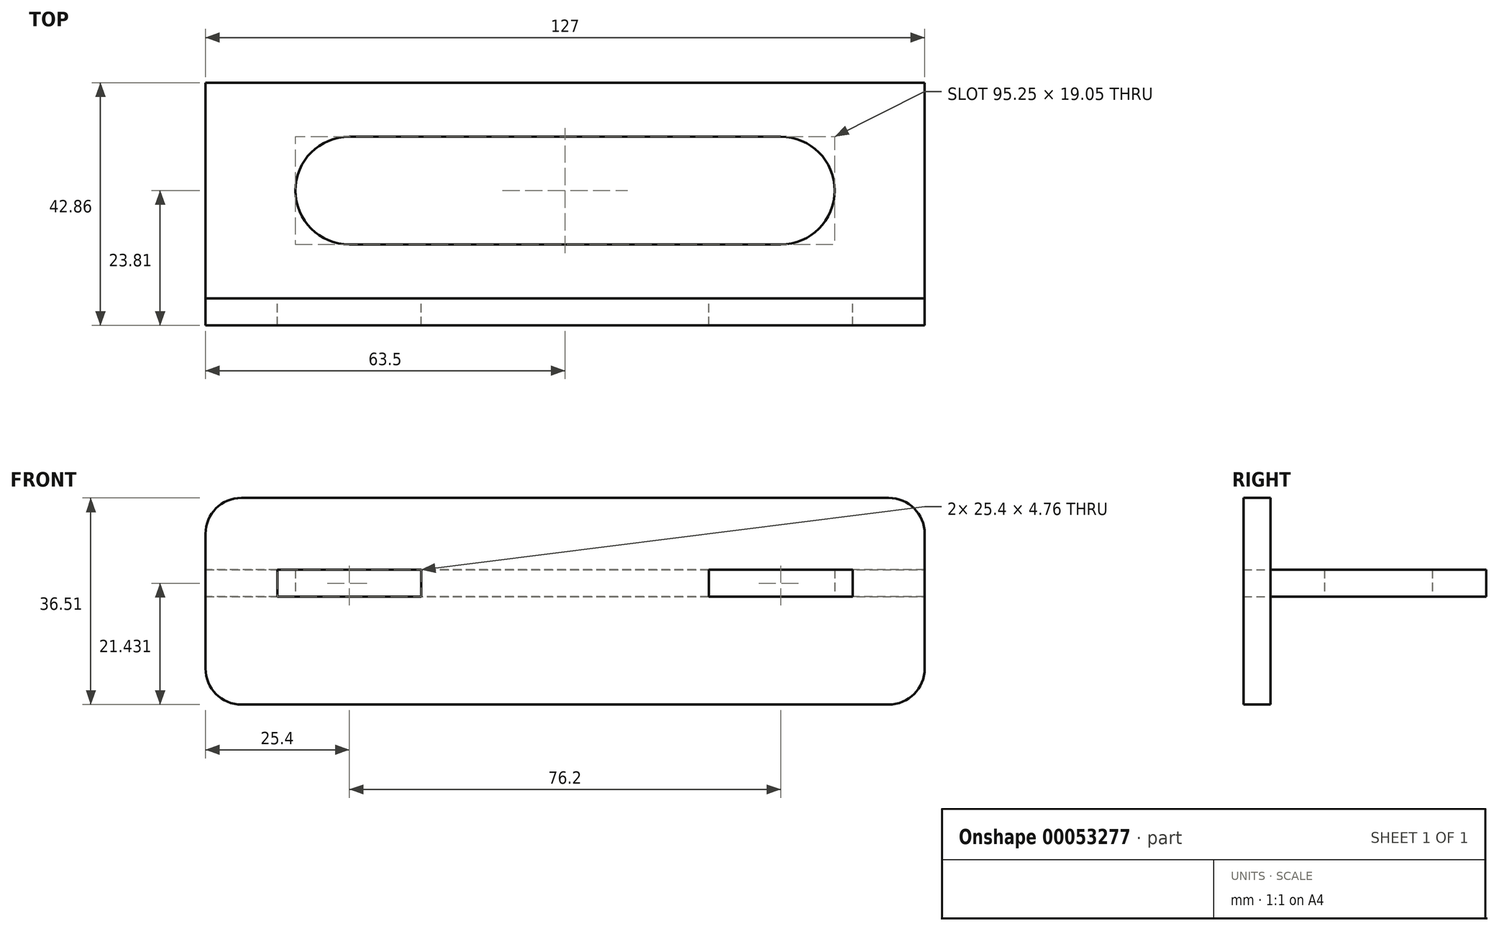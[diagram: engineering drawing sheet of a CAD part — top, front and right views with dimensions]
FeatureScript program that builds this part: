
annotation { "Feature Type Name" : "Feature", "Feature Type Description" : "" }
export const myFeature = defineFeature(function(context is Context, id is Id, definition is map)
    precondition{}
    {
        {
            var Q0;
            Q0=qCreatedBy(makeId("Top.planeOp"),FACE);
            var sketch = newSketch(context, id + "F0", { "sketchPlane" : qUnion([Q0])});
            skLineSegment(sketch, "E0", {"start": v(-101.6, 19.05) * mm, "end": v(25.4, 19.05) * mm});
            skLineSegment(sketch, "E1", {"start": v(25.4, 19.05) * mm, "end": v(25.4, -19.05) * mm});
            skLineSegment(sketch, "E2", {"start": v(25.4, -19.05) * mm, "end": v(12.7, -19.05) * mm});
            skLineSegment(sketch, "E3", {"start": v(12.7, -19.05) * mm, "end": v(12.7, -23.81) * mm});
            skLineSegment(sketch, "E4", {"start": v(12.7, -23.81) * mm, "end": v(-12.7, -23.81) * mm});
            skLineSegment(sketch, "E5", {"start": v(-12.7, -23.81) * mm, "end": v(-12.7, -19.05) * mm});
            skLineSegment(sketch, "E6", {"start": v(-12.7, -19.05) * mm, "end": v(-63.5, -19.05) * mm});
            skLineSegment(sketch, "E7", {"start": v(-63.5, -19.05) * mm, "end": v(-63.5, -23.81) * mm});
            skLineSegment(sketch, "E8", {"start": v(-63.5, -23.81) * mm, "end": v(-88.9, -23.81) * mm});
            skLineSegment(sketch, "E9", {"start": v(-88.9, -23.81) * mm, "end": v(-88.9, -19.05) * mm});
            skLineSegment(sketch, "E10", {"start": v(-88.9, -19.05) * mm, "end": v(-101.6, -19.05) * mm});
            skLineSegment(sketch, "E11", {"start": v(-101.6, -19.05) * mm, "end": v(-101.6, 19.05) * mm});
            skArc(sketch, "E12", {"start": v(-76.2, 9.53) * mm, "mid": v(-85.73, 0) * mm, "end": v(-76.2, -9.53) * mm});
            skArc(sketch, "E13", {"start": v(0, -9.53) * mm, "mid": v(9.53, 0) * mm, "end": v(0, 9.53) * mm});
            skLineSegment(sketch, "E14", {"start": v(-76.2, 9.53) * mm, "end": v(0, 9.53) * mm});
            skLineSegment(sketch, "E15", {"start": v(-76.2, -9.53) * mm, "end": v(0, -9.53) * mm});
            skSolve(sketch);
        }
        {
            var Q0;
            Q0=makeQuery(id+"F0.imprint","IMPRINT",FACE,{"disambiguationData":[TD([[makeQuery(id+"F0.imprint","IMPRINT",EDGE,{"derivedFrom":sQuery(id+"F0.wireOp",EDGE,"E0")}),-1.0]])]});
            extrude(context, id + "F1", {"entities" : qUnion([Q0]), "depth" : 4.76 * mm});
        }
        {
            var Q0;
            Q0=makeQuery(id+"F1.opExtrude","SWEPT_FACE",FACE,{"disambiguationData":[OSD([sQuery(id+"F0.wireOp",EDGE,"E6")])]});
            var sketch = newSketch(context, id + "F2", { "sketchPlane" : qUnion([Q0])});
            skLineSegment(sketch, "E16.0.0", {"start": v(-88.9, 0) * mm, "end": v(-63.5, 0) * mm});
            skLineSegment(sketch, "E16.0.1", {"start": v(-63.5, 0) * mm, "end": v(-63.5, 4.76) * mm});
            skLineSegment(sketch, "E16.0.2", {"start": v(-63.5, 4.76) * mm, "end": v(-88.9, 4.76) * mm});
            skLineSegment(sketch, "E16.0.3", {"start": v(-88.9, 4.76) * mm, "end": v(-88.9, 0) * mm});
            skLineSegment(sketch, "E17.0.0", {"start": v(-12.7, 0) * mm, "end": v(12.7, 0) * mm});
            skLineSegment(sketch, "E17.0.1", {"start": v(12.7, 0) * mm, "end": v(12.7, 4.76) * mm});
            skLineSegment(sketch, "E17.0.2", {"start": v(12.7, 4.76) * mm, "end": v(-12.7, 4.76) * mm});
            skLineSegment(sketch, "E17.0.3", {"start": v(-12.7, 4.76) * mm, "end": v(-12.7, 0) * mm});
            skLineSegment(sketch, "E18", {"start": v(-101.6, 11.11) * mm, "end": v(-101.6, -12.7) * mm});
            skLineSegment(sketch, "E19", {"start": v(-95.25, -19.05) * mm, "end": v(19.05, -19.05) * mm});
            skLineSegment(sketch, "E20", {"start": v(25.4, -12.7) * mm, "end": v(25.4, 11.11) * mm});
            skLineSegment(sketch, "E21", {"start": v(19.05, 17.46) * mm, "end": v(-95.25, 17.46) * mm});
            skPoint(sketch, "E22.visualSharp", {"position": v(-101.6, 17.46) * mm});
            skArc(sketch, "E22.filletArc", {"start": v(-95.25, 17.46) * mm, "mid": v(-99.74, 15.6) * mm, "end": v(-101.6, 11.11) * mm});
            skPoint(sketch, "E23.visualSharp", {"position": v(-101.6, -19.05) * mm});
            skArc(sketch, "E23.filletArc", {"start": v(-101.6, -12.7) * mm, "mid": v(-99.74, -17.2) * mm, "end": v(-95.25, -19.05) * mm});
            skPoint(sketch, "E24.visualSharp", {"position": v(25.4, -19.05) * mm});
            skArc(sketch, "E24.filletArc", {"start": v(19.05, -19.05) * mm, "mid": v(23.54, -17.2) * mm, "end": v(25.4, -12.7) * mm});
            skPoint(sketch, "E25.visualSharp", {"position": v(25.4, 17.46) * mm});
            skArc(sketch, "E25.filletArc", {"start": v(25.4, 11.11) * mm, "mid": v(23.54, 15.6) * mm, "end": v(19.05, 17.46) * mm});
            skSolve(sketch);
        }
        {
            var Q0;
            Q0=makeQuery(id+"F2.imprint","IMPRINT",FACE,{"disambiguationData":[TD([[makeQuery(id+"F2.imprint","IMPRINT",EDGE,{"derivedFrom":sQuery(id+"F2.wireOp",EDGE,"E16.0.1")}),1.0]])]});
            var Q1;
            Q1=makeQuery(id+"F2.imprint","IMPRINT",FACE,{"disambiguationData":[TD([[makeQuery(id+"F2.imprint","IMPRINT",EDGE,{"derivedFrom":sQuery(id+"F2.wireOp",EDGE,"E16.0.0")}),-1.0]])]});
            extrude(context, id + "F3", {"entities" : qUnion([Q0, Q1]), "depth" : 4.76 * mm});
        }
    });
